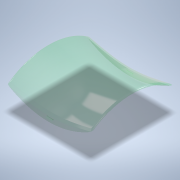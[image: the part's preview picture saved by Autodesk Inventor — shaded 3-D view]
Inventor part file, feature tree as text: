
AUTODESK INVENTOR PART (.ipt)
format: ipt  version: 2020.3 (Build 243373000, 373)  size: 507,392 bytes
history: native  units: mm
features: sketch x4, chamfer x3, extrude x2, fillet x2, projected_geometry x2, sweep x1, plane x1, mirror x1
ambient origin geometry x8: Origin, YZ Plane, XZ Plane, XY Plane, X Axis, Y Axis, Z Axis, Center Point
bodies: Body1 (feature_tree)
feature tree (16):
  sweep  "Sweep1"
  extrude  "Extrusion4"  Depth=4.0mm TaperAngle=45.0deg
  chamfer  "Chamfer1"  Distance=142.009mm
  plane  "Work Plane8"
  mirror  "Mirror2"
  extrude  "Extrusion5"  Depth=3.0mm
  fillet  "Fillet3"  Radius=1.0mm
  chamfer  "Chamfer2"  Distance=1.0mm Angle=45.0deg
  chamfer  "Chamfer3"  Distance=200.0mm
  fillet  "Fillet4"  [1 undecoded]
  sketch  "Sketch2"  dims[d16=0.0mm d17=0.0mm d18=10.0mm]
  sketch  "Sketch6"  dims[d19=4.0mm d20=0.0mm d21=4.0mm d22=2.0mm d23=45.0deg]
  sketch  "Sketch7"  dims[d24=5.0mm]
  projected_geometry  "Projected Loop1"
  sketch  "Sketch8"  dims[d25=2.0mm d26=142.009mm d27=0.0mm d28=3.0mm d29=1.0mm d30=2.0mm d31=45.0deg d32=1.0mm d33=2.0mm d34=45.0deg d35=200.0mm]
  projected_geometry  "Projected Loop2"
note: 1 required parameter value undecoded (feature->parameter linkage not recoverable at this tier; creation-order binding heuristic only, values carry confidence <= 0.55)
